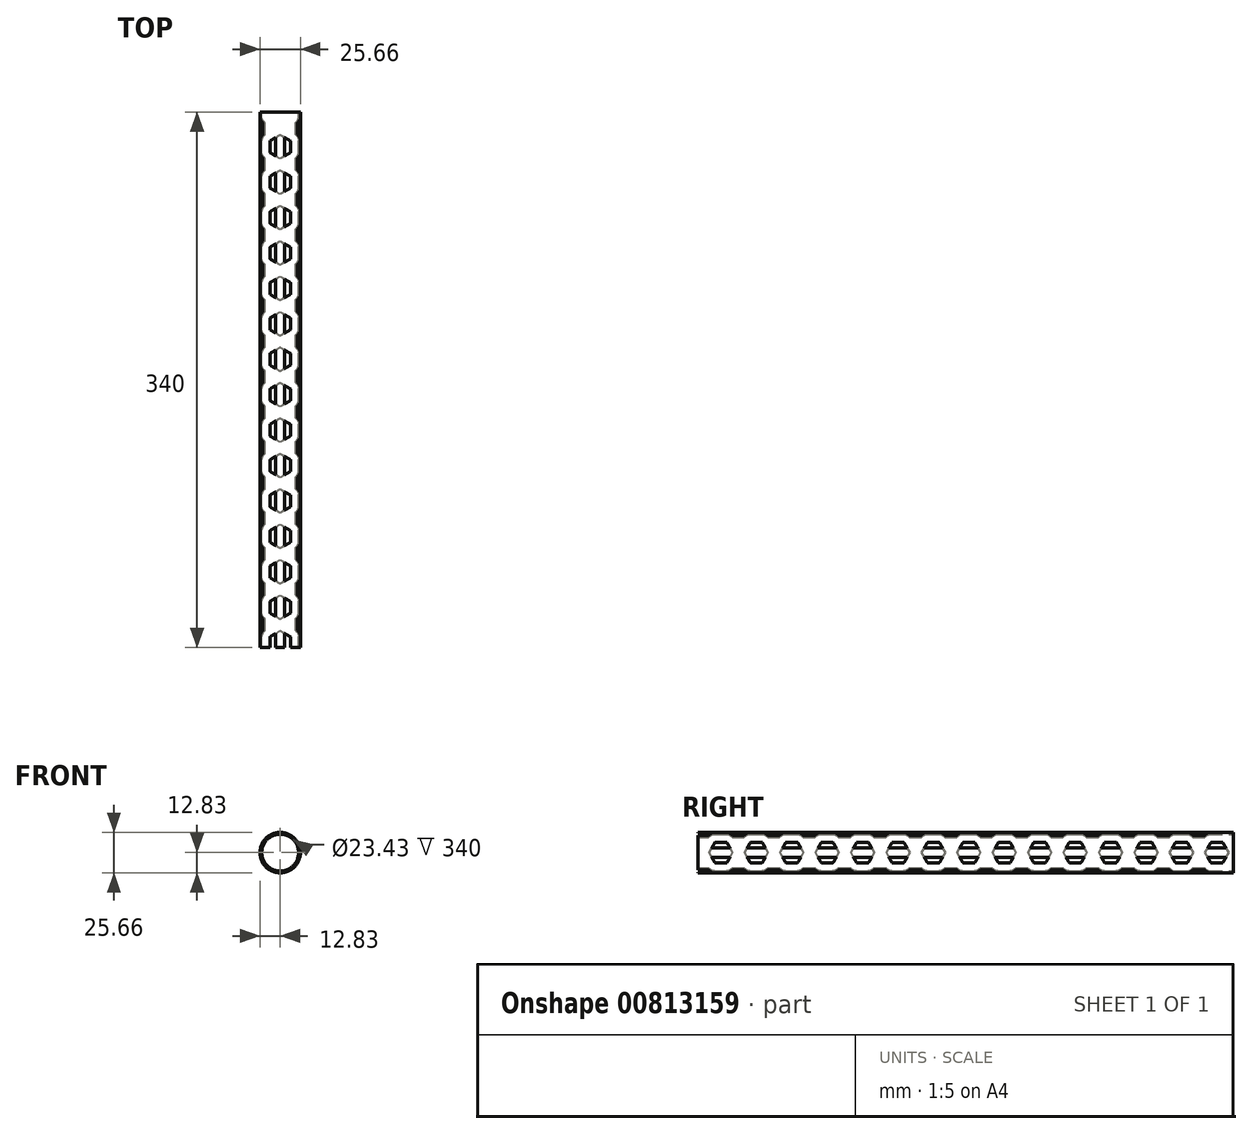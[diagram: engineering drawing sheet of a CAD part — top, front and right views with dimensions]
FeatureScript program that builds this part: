
annotation { "Feature Type Name" : "Feature", "Feature Type Description" : "" }
export const myFeature = defineFeature(function(context is Context, id is Id, definition is map)
    precondition{}
    {
        {
            var Q0;
            Q0=qCreatedBy(makeId("Front.planeOp"),FACE);
            var sketch = newSketch(context, id + "F0", { "sketchPlane" : qUnion([Q0])});
            skCircle(sketch, "E0", {"center": v(0, 0) * mm, "radius": 12.83 * mm});
            skCircle(sketch, "E1", {"center": v(0, 0) * mm, "radius": 11.72 * mm});
            skSolve(sketch);
        }
        {
            var Q0;
            Q0=makeQuery(id+"F0.imprint","IMPRINT",FACE,{"disambiguationData":[TD([[makeQuery(id+"F0.imprint","IMPRINT",EDGE,{"derivedFrom":sQuery(id+"F0.wireOp",EDGE,"E0")}),1.0]])]});
            var Q1;
            Q1=sQuery(id+"F0.wireOp",EDGE,"E1");
            var Q2;
            Q2=sQuery(id+"F0.wireOp",EDGE,"E0");
            extrude(context, id + "F1", {"entities" : qUnion([Q0]), "surfaceEntities" : qUnion([Q1, Q2]), "endBound" : BoundingType.SYMMETRIC, "depth" : 340 * mm, "offsetDistance" : 25 * mm});
        }
        {
            var Q0;
            Q0=qCreatedBy(makeId("Right.planeOp"),FACE);
            var sketch = newSketch(context, id + "F2", { "sketchPlane" : qUnion([Q0])});
            skCircle(sketch, "E2.cCircle", {"center": v(159.5, 0) * mm, "radius": 6.5 * mm, "construction": true});
            skLineSegment(sketch, "E2.0", {"start": v(155.75, 6.5) * mm, "end": v(163.25, 6.5) * mm});
            skLineSegment(sketch, "E2.1", {"start": v(163.25, 6.5) * mm, "end": v(167, 0) * mm});
            skLineSegment(sketch, "E2.2", {"start": v(167, 0) * mm, "end": v(163.25, -6.5) * mm});
            skLineSegment(sketch, "E2.3", {"start": v(163.25, -6.5) * mm, "end": v(155.75, -6.5) * mm});
            skLineSegment(sketch, "E2.4", {"start": v(155.75, -6.5) * mm, "end": v(152, 0) * mm});
            skLineSegment(sketch, "E2.5", {"start": v(152, 0) * mm, "end": v(155.75, 6.5) * mm});
            skPoint(sketch, "E2.0.midPoint", {"position": v(159.5, 6.5) * mm});
            skCircle(sketch, "E3.cCircle", {"center": v(137, 0) * mm, "radius": 6.5 * mm, "construction": true});
            skLineSegment(sketch, "E3.0", {"start": v(133.25, 6.5) * mm, "end": v(140.75, 6.5) * mm});
            skLineSegment(sketch, "E3.1", {"start": v(140.75, 6.5) * mm, "end": v(144.5, 0) * mm});
            skLineSegment(sketch, "E3.2", {"start": v(144.5, 0) * mm, "end": v(140.75, -6.5) * mm});
            skLineSegment(sketch, "E3.3", {"start": v(140.75, -6.5) * mm, "end": v(133.25, -6.5) * mm});
            skLineSegment(sketch, "E3.4", {"start": v(133.25, -6.5) * mm, "end": v(129.5, 0) * mm});
            skLineSegment(sketch, "E3.5", {"start": v(129.5, 0) * mm, "end": v(133.25, 6.5) * mm});
            skPoint(sketch, "E3.0.midPoint", {"position": v(137, 6.5) * mm});
            skCircle(sketch, "E4.cCircle", {"center": v(114.5, 0) * mm, "radius": 6.5 * mm, "construction": true});
            skLineSegment(sketch, "E4.0", {"start": v(110.75, 6.5) * mm, "end": v(118.25, 6.5) * mm});
            skLineSegment(sketch, "E4.1", {"start": v(118.25, 6.5) * mm, "end": v(122, 0) * mm});
            skLineSegment(sketch, "E4.2", {"start": v(122, 0) * mm, "end": v(118.25, -6.5) * mm});
            skLineSegment(sketch, "E4.3", {"start": v(118.25, -6.5) * mm, "end": v(110.75, -6.5) * mm});
            skLineSegment(sketch, "E4.4", {"start": v(110.75, -6.5) * mm, "end": v(107, 0) * mm});
            skLineSegment(sketch, "E4.5", {"start": v(107, 0) * mm, "end": v(110.75, 6.5) * mm});
            skPoint(sketch, "E4.0.midPoint", {"position": v(114.5, 6.5) * mm});
            skCircle(sketch, "E5.cCircle", {"center": v(92, 0) * mm, "radius": 6.5 * mm, "construction": true});
            skLineSegment(sketch, "E5.0", {"start": v(88.25, 6.5) * mm, "end": v(95.75, 6.5) * mm});
            skLineSegment(sketch, "E5.1", {"start": v(95.75, 6.5) * mm, "end": v(99.5, 0) * mm});
            skLineSegment(sketch, "E5.2", {"start": v(99.5, 0) * mm, "end": v(95.75, -6.5) * mm});
            skLineSegment(sketch, "E5.3", {"start": v(95.75, -6.5) * mm, "end": v(88.25, -6.5) * mm});
            skLineSegment(sketch, "E5.4", {"start": v(88.25, -6.5) * mm, "end": v(84.5, 0) * mm});
            skLineSegment(sketch, "E5.5", {"start": v(84.5, 0) * mm, "end": v(88.25, 6.5) * mm});
            skPoint(sketch, "E5.0.midPoint", {"position": v(92, 6.5) * mm});
            skCircle(sketch, "E6.cCircle", {"center": v(69.5, 0) * mm, "radius": 6.5 * mm, "construction": true});
            skLineSegment(sketch, "E6.0", {"start": v(65.75, 6.5) * mm, "end": v(73.25, 6.5) * mm});
            skLineSegment(sketch, "E6.1", {"start": v(73.25, 6.5) * mm, "end": v(77, 0) * mm});
            skLineSegment(sketch, "E6.2", {"start": v(77, 0) * mm, "end": v(73.25, -6.5) * mm});
            skLineSegment(sketch, "E6.3", {"start": v(73.25, -6.5) * mm, "end": v(65.75, -6.5) * mm});
            skLineSegment(sketch, "E6.4", {"start": v(65.75, -6.5) * mm, "end": v(62, 0) * mm});
            skLineSegment(sketch, "E6.5", {"start": v(62, 0) * mm, "end": v(65.75, 6.5) * mm});
            skPoint(sketch, "E6.0.midPoint", {"position": v(69.5, 6.5) * mm});
            skCircle(sketch, "E7.cCircle", {"center": v(47, 0) * mm, "radius": 6.5 * mm, "construction": true});
            skLineSegment(sketch, "E7.0", {"start": v(43.25, 6.5) * mm, "end": v(50.75, 6.5) * mm});
            skLineSegment(sketch, "E7.1", {"start": v(50.75, 6.5) * mm, "end": v(54.5, 0) * mm});
            skLineSegment(sketch, "E7.2", {"start": v(54.5, 0) * mm, "end": v(50.75, -6.5) * mm});
            skLineSegment(sketch, "E7.3", {"start": v(50.75, -6.5) * mm, "end": v(43.25, -6.5) * mm});
            skLineSegment(sketch, "E7.4", {"start": v(43.25, -6.5) * mm, "end": v(39.5, 0) * mm});
            skLineSegment(sketch, "E7.5", {"start": v(39.5, 0) * mm, "end": v(43.25, 6.5) * mm});
            skPoint(sketch, "E7.0.midPoint", {"position": v(47, 6.5) * mm});
            skCircle(sketch, "E8.cCircle", {"center": v(24.5, 0) * mm, "radius": 6.5 * mm, "construction": true});
            skLineSegment(sketch, "E8.0", {"start": v(20.75, 6.5) * mm, "end": v(28.25, 6.5) * mm});
            skLineSegment(sketch, "E8.1", {"start": v(28.25, 6.5) * mm, "end": v(32, 0) * mm});
            skLineSegment(sketch, "E8.2", {"start": v(32, 0) * mm, "end": v(28.25, -6.5) * mm});
            skLineSegment(sketch, "E8.3", {"start": v(28.25, -6.5) * mm, "end": v(20.75, -6.5) * mm});
            skLineSegment(sketch, "E8.4", {"start": v(20.75, -6.5) * mm, "end": v(17, 0) * mm});
            skLineSegment(sketch, "E8.5", {"start": v(17, 0) * mm, "end": v(20.75, 6.5) * mm});
            skPoint(sketch, "E8.0.midPoint", {"position": v(24.5, 6.5) * mm});
            skCircle(sketch, "E9.cCircle", {"center": v(2, 0) * mm, "radius": 6.5 * mm, "construction": true});
            skLineSegment(sketch, "E9.0", {"start": v(-1.75, 6.5) * mm, "end": v(5.75, 6.5) * mm});
            skLineSegment(sketch, "E9.1", {"start": v(5.75, 6.5) * mm, "end": v(9.5, 0) * mm});
            skLineSegment(sketch, "E9.2", {"start": v(9.5, 0) * mm, "end": v(5.75, -6.5) * mm});
            skLineSegment(sketch, "E9.3", {"start": v(5.75, -6.5) * mm, "end": v(-1.75, -6.5) * mm});
            skLineSegment(sketch, "E9.4", {"start": v(-1.75, -6.5) * mm, "end": v(-5.5, 0) * mm});
            skLineSegment(sketch, "E9.5", {"start": v(-5.5, 0) * mm, "end": v(-1.75, 6.5) * mm});
            skPoint(sketch, "E9.0.midPoint", {"position": v(2, 6.5) * mm});
            skCircle(sketch, "E10.cCircle", {"center": v(-20.5, 0) * mm, "radius": 6.5 * mm, "construction": true});
            skLineSegment(sketch, "E10.0", {"start": v(-24.25, 6.5) * mm, "end": v(-16.75, 6.5) * mm});
            skLineSegment(sketch, "E10.1", {"start": v(-16.75, 6.5) * mm, "end": v(-13, 0) * mm});
            skLineSegment(sketch, "E10.2", {"start": v(-13, 0) * mm, "end": v(-16.75, -6.5) * mm});
            skLineSegment(sketch, "E10.3", {"start": v(-16.75, -6.5) * mm, "end": v(-24.25, -6.5) * mm});
            skLineSegment(sketch, "E10.4", {"start": v(-24.25, -6.5) * mm, "end": v(-28, 0) * mm});
            skLineSegment(sketch, "E10.5", {"start": v(-28, 0) * mm, "end": v(-24.25, 6.5) * mm});
            skPoint(sketch, "E10.0.midPoint", {"position": v(-20.5, 6.5) * mm});
            skCircle(sketch, "E11.cCircle", {"center": v(-43, 0) * mm, "radius": 6.5 * mm, "construction": true});
            skLineSegment(sketch, "E11.0", {"start": v(-46.75, 6.5) * mm, "end": v(-39.25, 6.5) * mm});
            skLineSegment(sketch, "E11.1", {"start": v(-39.25, 6.5) * mm, "end": v(-35.5, 0) * mm});
            skLineSegment(sketch, "E11.2", {"start": v(-35.5, 0) * mm, "end": v(-39.25, -6.5) * mm});
            skLineSegment(sketch, "E11.3", {"start": v(-39.25, -6.5) * mm, "end": v(-46.75, -6.5) * mm});
            skLineSegment(sketch, "E11.4", {"start": v(-46.75, -6.5) * mm, "end": v(-50.5, 0) * mm});
            skLineSegment(sketch, "E11.5", {"start": v(-50.5, 0) * mm, "end": v(-46.75, 6.5) * mm});
            skPoint(sketch, "E11.0.midPoint", {"position": v(-43, 6.5) * mm});
            skCircle(sketch, "E12.cCircle", {"center": v(-65.5, 0) * mm, "radius": 6.5 * mm, "construction": true});
            skLineSegment(sketch, "E12.0", {"start": v(-69.25, 6.5) * mm, "end": v(-61.75, 6.5) * mm});
            skLineSegment(sketch, "E12.1", {"start": v(-61.75, 6.5) * mm, "end": v(-58, 0) * mm});
            skLineSegment(sketch, "E12.2", {"start": v(-58, 0) * mm, "end": v(-61.75, -6.5) * mm});
            skLineSegment(sketch, "E12.3", {"start": v(-61.75, -6.5) * mm, "end": v(-69.25, -6.5) * mm});
            skLineSegment(sketch, "E12.4", {"start": v(-69.25, -6.5) * mm, "end": v(-73, 0) * mm});
            skLineSegment(sketch, "E12.5", {"start": v(-73, 0) * mm, "end": v(-69.25, 6.5) * mm});
            skPoint(sketch, "E12.0.midPoint", {"position": v(-65.5, 6.5) * mm});
            skCircle(sketch, "E13.cCircle", {"center": v(-88, 0) * mm, "radius": 6.5 * mm, "construction": true});
            skLineSegment(sketch, "E13.0", {"start": v(-91.75, 6.5) * mm, "end": v(-84.25, 6.5) * mm});
            skLineSegment(sketch, "E13.1", {"start": v(-84.25, 6.5) * mm, "end": v(-80.5, 0) * mm});
            skLineSegment(sketch, "E13.2", {"start": v(-80.5, 0) * mm, "end": v(-84.25, -6.5) * mm});
            skLineSegment(sketch, "E13.3", {"start": v(-84.25, -6.5) * mm, "end": v(-91.75, -6.5) * mm});
            skLineSegment(sketch, "E13.4", {"start": v(-91.75, -6.5) * mm, "end": v(-95.5, 0) * mm});
            skLineSegment(sketch, "E13.5", {"start": v(-95.5, 0) * mm, "end": v(-91.75, 6.5) * mm});
            skPoint(sketch, "E13.0.midPoint", {"position": v(-88, 6.5) * mm});
            skCircle(sketch, "E14.cCircle", {"center": v(-110.5, 0) * mm, "radius": 6.5 * mm, "construction": true});
            skLineSegment(sketch, "E14.0", {"start": v(-114.25, 6.5) * mm, "end": v(-106.75, 6.5) * mm});
            skLineSegment(sketch, "E14.1", {"start": v(-106.75, 6.5) * mm, "end": v(-103, 0) * mm});
            skLineSegment(sketch, "E14.2", {"start": v(-103, 0) * mm, "end": v(-106.75, -6.5) * mm});
            skLineSegment(sketch, "E14.3", {"start": v(-106.75, -6.5) * mm, "end": v(-114.25, -6.5) * mm});
            skLineSegment(sketch, "E14.4", {"start": v(-114.25, -6.5) * mm, "end": v(-118, 0) * mm});
            skLineSegment(sketch, "E14.5", {"start": v(-118, 0) * mm, "end": v(-114.25, 6.5) * mm});
            skPoint(sketch, "E14.0.midPoint", {"position": v(-110.5, 6.5) * mm});
            skCircle(sketch, "E15.cCircle", {"center": v(-133, 0) * mm, "radius": 6.5 * mm, "construction": true});
            skLineSegment(sketch, "E15.0", {"start": v(-136.75, 6.5) * mm, "end": v(-129.25, 6.5) * mm});
            skLineSegment(sketch, "E15.1", {"start": v(-129.25, 6.5) * mm, "end": v(-125.5, 0) * mm});
            skLineSegment(sketch, "E15.2", {"start": v(-125.5, 0) * mm, "end": v(-129.25, -6.5) * mm});
            skLineSegment(sketch, "E15.3", {"start": v(-129.25, -6.5) * mm, "end": v(-136.75, -6.5) * mm});
            skLineSegment(sketch, "E15.4", {"start": v(-136.75, -6.5) * mm, "end": v(-140.5, 0) * mm});
            skLineSegment(sketch, "E15.5", {"start": v(-140.5, 0) * mm, "end": v(-136.75, 6.5) * mm});
            skPoint(sketch, "E15.0.midPoint", {"position": v(-133, 6.5) * mm});
            skCircle(sketch, "E16.cCircle", {"center": v(-155.5, 0) * mm, "radius": 6.5 * mm, "construction": true});
            skLineSegment(sketch, "E16.0", {"start": v(-159.25, 6.5) * mm, "end": v(-151.75, 6.5) * mm});
            skLineSegment(sketch, "E16.1", {"start": v(-151.75, 6.5) * mm, "end": v(-148, 0) * mm});
            skLineSegment(sketch, "E16.2", {"start": v(-148, 0) * mm, "end": v(-151.75, -6.5) * mm});
            skLineSegment(sketch, "E16.3", {"start": v(-151.75, -6.5) * mm, "end": v(-159.25, -6.5) * mm});
            skLineSegment(sketch, "E16.4", {"start": v(-159.25, -6.5) * mm, "end": v(-163, 0) * mm});
            skLineSegment(sketch, "E16.5", {"start": v(-163, 0) * mm, "end": v(-159.25, 6.5) * mm});
            skPoint(sketch, "E16.0.midPoint", {"position": v(-155.5, 6.5) * mm});
            skSolve(sketch);
        }
        {
            var Q0;
            Q0 = qSketchRegion(id + "F2", true);
            extrude(context, id + "F3", {"entities" : qUnion([Q0]), "operationType" : NewBodyOperationType.REMOVE, "endBound" : BoundingType.SYMMETRIC, "depth" : 25 * mm, "offsetDistance" : 25 * mm});
        }
        {
            var Q0;
            Q0=qCreatedBy(makeId("Top.planeOp"),FACE);
            var sketch = newSketch(context, id + "F4", { "sketchPlane" : qUnion([Q0])});
            skCircle(sketch, "E17.cCircle", {"center": v(0, -166.98) * mm, "radius": 6.5 * mm, "construction": true});
            skLineSegment(sketch, "E17.0", {"start": v(6.5, -163.23) * mm, "end": v(6.5, -170.73) * mm});
            skLineSegment(sketch, "E17.1", {"start": v(6.5, -170.73) * mm, "end": v(0, -174.48) * mm});
            skLineSegment(sketch, "E17.2", {"start": v(0, -174.48) * mm, "end": v(-6.5, -170.73) * mm});
            skLineSegment(sketch, "E17.3", {"start": v(-6.5, -170.73) * mm, "end": v(-6.5, -163.23) * mm});
            skLineSegment(sketch, "E17.4", {"start": v(-6.5, -163.23) * mm, "end": v(0, -159.48) * mm});
            skLineSegment(sketch, "E17.5", {"start": v(0, -159.48) * mm, "end": v(6.5, -163.23) * mm});
            skPoint(sketch, "E17.0.midPoint", {"position": v(6.5, -166.98) * mm});
            skCircle(sketch, "E18.cCircle", {"center": v(0, -144.48) * mm, "radius": 6.5 * mm, "construction": true});
            skLineSegment(sketch, "E18.0", {"start": v(6.5, -140.73) * mm, "end": v(6.5, -148.23) * mm});
            skLineSegment(sketch, "E18.1", {"start": v(6.5, -148.23) * mm, "end": v(0, -151.98) * mm});
            skLineSegment(sketch, "E18.2", {"start": v(0, -151.98) * mm, "end": v(-6.5, -148.23) * mm});
            skLineSegment(sketch, "E18.3", {"start": v(-6.5, -148.23) * mm, "end": v(-6.5, -140.73) * mm});
            skLineSegment(sketch, "E18.4", {"start": v(-6.5, -140.73) * mm, "end": v(0, -136.98) * mm});
            skLineSegment(sketch, "E18.5", {"start": v(0, -136.98) * mm, "end": v(6.5, -140.73) * mm});
            skPoint(sketch, "E18.0.midPoint", {"position": v(6.5, -144.48) * mm});
            skCircle(sketch, "E19.cCircle", {"center": v(0, -121.98) * mm, "radius": 6.5 * mm, "construction": true});
            skLineSegment(sketch, "E19.0", {"start": v(6.5, -118.23) * mm, "end": v(6.5, -125.73) * mm});
            skLineSegment(sketch, "E19.1", {"start": v(6.5, -125.73) * mm, "end": v(0, -129.48) * mm});
            skLineSegment(sketch, "E19.2", {"start": v(0, -129.48) * mm, "end": v(-6.5, -125.73) * mm});
            skLineSegment(sketch, "E19.3", {"start": v(-6.5, -125.73) * mm, "end": v(-6.5, -118.23) * mm});
            skLineSegment(sketch, "E19.4", {"start": v(-6.5, -118.23) * mm, "end": v(0, -114.48) * mm});
            skLineSegment(sketch, "E19.5", {"start": v(0, -114.48) * mm, "end": v(6.5, -118.23) * mm});
            skPoint(sketch, "E19.0.midPoint", {"position": v(6.5, -121.98) * mm});
            skCircle(sketch, "E20.cCircle", {"center": v(0, -99.48) * mm, "radius": 6.5 * mm, "construction": true});
            skLineSegment(sketch, "E20.0", {"start": v(6.5, -95.73) * mm, "end": v(6.5, -103.23) * mm});
            skLineSegment(sketch, "E20.1", {"start": v(6.5, -103.23) * mm, "end": v(0, -106.98) * mm});
            skLineSegment(sketch, "E20.2", {"start": v(0, -106.98) * mm, "end": v(-6.5, -103.23) * mm});
            skLineSegment(sketch, "E20.3", {"start": v(-6.5, -103.23) * mm, "end": v(-6.5, -95.73) * mm});
            skLineSegment(sketch, "E20.4", {"start": v(-6.5, -95.73) * mm, "end": v(0, -91.98) * mm});
            skLineSegment(sketch, "E20.5", {"start": v(0, -91.98) * mm, "end": v(6.5, -95.73) * mm});
            skPoint(sketch, "E20.0.midPoint", {"position": v(6.5, -99.48) * mm});
            skCircle(sketch, "E21.cCircle", {"center": v(0, -76.98) * mm, "radius": 6.5 * mm, "construction": true});
            skLineSegment(sketch, "E21.0", {"start": v(6.5, -73.23) * mm, "end": v(6.5, -80.73) * mm});
            skLineSegment(sketch, "E21.1", {"start": v(6.5, -80.73) * mm, "end": v(0, -84.48) * mm});
            skLineSegment(sketch, "E21.2", {"start": v(0, -84.48) * mm, "end": v(-6.5, -80.73) * mm});
            skLineSegment(sketch, "E21.3", {"start": v(-6.5, -80.73) * mm, "end": v(-6.5, -73.23) * mm});
            skLineSegment(sketch, "E21.4", {"start": v(-6.5, -73.23) * mm, "end": v(0, -69.48) * mm});
            skLineSegment(sketch, "E21.5", {"start": v(0, -69.48) * mm, "end": v(6.5, -73.23) * mm});
            skPoint(sketch, "E21.0.midPoint", {"position": v(6.5, -76.98) * mm});
            skCircle(sketch, "E22.cCircle", {"center": v(0, -54.48) * mm, "radius": 6.5 * mm, "construction": true});
            skLineSegment(sketch, "E22.0", {"start": v(6.5, -50.73) * mm, "end": v(6.5, -58.23) * mm});
            skLineSegment(sketch, "E22.1", {"start": v(6.5, -58.23) * mm, "end": v(0, -61.98) * mm});
            skLineSegment(sketch, "E22.2", {"start": v(0, -61.98) * mm, "end": v(-6.5, -58.23) * mm});
            skLineSegment(sketch, "E22.3", {"start": v(-6.5, -58.23) * mm, "end": v(-6.5, -50.73) * mm});
            skLineSegment(sketch, "E22.4", {"start": v(-6.5, -50.73) * mm, "end": v(0, -46.98) * mm});
            skLineSegment(sketch, "E22.5", {"start": v(0, -46.98) * mm, "end": v(6.5, -50.73) * mm});
            skPoint(sketch, "E22.0.midPoint", {"position": v(6.5, -54.48) * mm});
            skCircle(sketch, "E23.cCircle", {"center": v(0, -31.98) * mm, "radius": 6.5 * mm, "construction": true});
            skLineSegment(sketch, "E23.0", {"start": v(6.5, -28.23) * mm, "end": v(6.5, -35.73) * mm});
            skLineSegment(sketch, "E23.1", {"start": v(6.5, -35.73) * mm, "end": v(0, -39.48) * mm});
            skLineSegment(sketch, "E23.2", {"start": v(0, -39.48) * mm, "end": v(-6.5, -35.73) * mm});
            skLineSegment(sketch, "E23.3", {"start": v(-6.5, -35.73) * mm, "end": v(-6.5, -28.23) * mm});
            skLineSegment(sketch, "E23.4", {"start": v(-6.5, -28.23) * mm, "end": v(0, -24.48) * mm});
            skLineSegment(sketch, "E23.5", {"start": v(0, -24.48) * mm, "end": v(6.5, -28.23) * mm});
            skPoint(sketch, "E23.0.midPoint", {"position": v(6.5, -31.98) * mm});
            skCircle(sketch, "E24.cCircle", {"center": v(0, -9.48) * mm, "radius": 6.5 * mm, "construction": true});
            skLineSegment(sketch, "E24.0", {"start": v(6.5, -5.73) * mm, "end": v(6.5, -13.23) * mm});
            skLineSegment(sketch, "E24.1", {"start": v(6.5, -13.23) * mm, "end": v(0, -16.98) * mm});
            skLineSegment(sketch, "E24.2", {"start": v(0, -16.98) * mm, "end": v(-6.5, -13.23) * mm});
            skLineSegment(sketch, "E24.3", {"start": v(-6.5, -13.23) * mm, "end": v(-6.5, -5.73) * mm});
            skLineSegment(sketch, "E24.4", {"start": v(-6.5, -5.73) * mm, "end": v(0, -1.98) * mm});
            skLineSegment(sketch, "E24.5", {"start": v(0, -1.98) * mm, "end": v(6.5, -5.73) * mm});
            skPoint(sketch, "E24.0.midPoint", {"position": v(6.5, -9.48) * mm});
            skCircle(sketch, "E25.cCircle", {"center": v(0, 13.02) * mm, "radius": 6.5 * mm, "construction": true});
            skLineSegment(sketch, "E25.0", {"start": v(6.5, 16.77) * mm, "end": v(6.5, 9.27) * mm});
            skLineSegment(sketch, "E25.1", {"start": v(6.5, 9.27) * mm, "end": v(0, 5.52) * mm});
            skLineSegment(sketch, "E25.2", {"start": v(0, 5.52) * mm, "end": v(-6.5, 9.27) * mm});
            skLineSegment(sketch, "E25.3", {"start": v(-6.5, 9.27) * mm, "end": v(-6.5, 16.77) * mm});
            skLineSegment(sketch, "E25.4", {"start": v(-6.5, 16.77) * mm, "end": v(0, 20.52) * mm});
            skLineSegment(sketch, "E25.5", {"start": v(0, 20.52) * mm, "end": v(6.5, 16.77) * mm});
            skPoint(sketch, "E25.0.midPoint", {"position": v(6.5, 13.02) * mm});
            skCircle(sketch, "E26.cCircle", {"center": v(0, 35.52) * mm, "radius": 6.5 * mm, "construction": true});
            skLineSegment(sketch, "E26.0", {"start": v(6.5, 39.27) * mm, "end": v(6.5, 31.77) * mm});
            skLineSegment(sketch, "E26.1", {"start": v(6.5, 31.77) * mm, "end": v(0, 28.02) * mm});
            skLineSegment(sketch, "E26.2", {"start": v(0, 28.02) * mm, "end": v(-6.5, 31.77) * mm});
            skLineSegment(sketch, "E26.3", {"start": v(-6.5, 31.77) * mm, "end": v(-6.5, 39.27) * mm});
            skLineSegment(sketch, "E26.4", {"start": v(-6.5, 39.27) * mm, "end": v(0, 43.02) * mm});
            skLineSegment(sketch, "E26.5", {"start": v(0, 43.02) * mm, "end": v(6.5, 39.27) * mm});
            skPoint(sketch, "E26.0.midPoint", {"position": v(6.5, 35.52) * mm});
            skCircle(sketch, "E27.cCircle", {"center": v(0, 58.02) * mm, "radius": 6.5 * mm, "construction": true});
            skLineSegment(sketch, "E27.0", {"start": v(6.5, 61.77) * mm, "end": v(6.5, 54.27) * mm});
            skLineSegment(sketch, "E27.1", {"start": v(6.5, 54.27) * mm, "end": v(0, 50.52) * mm});
            skLineSegment(sketch, "E27.2", {"start": v(0, 50.52) * mm, "end": v(-6.5, 54.27) * mm});
            skLineSegment(sketch, "E27.3", {"start": v(-6.5, 54.27) * mm, "end": v(-6.5, 61.77) * mm});
            skLineSegment(sketch, "E27.4", {"start": v(-6.5, 61.77) * mm, "end": v(0, 65.52) * mm});
            skLineSegment(sketch, "E27.5", {"start": v(0, 65.52) * mm, "end": v(6.5, 61.77) * mm});
            skPoint(sketch, "E27.0.midPoint", {"position": v(6.5, 58.02) * mm});
            skCircle(sketch, "E28.cCircle", {"center": v(0, 80.52) * mm, "radius": 6.5 * mm, "construction": true});
            skLineSegment(sketch, "E28.0", {"start": v(6.5, 84.27) * mm, "end": v(6.5, 76.77) * mm});
            skLineSegment(sketch, "E28.1", {"start": v(6.5, 76.77) * mm, "end": v(0, 73.02) * mm});
            skLineSegment(sketch, "E28.2", {"start": v(0, 73.02) * mm, "end": v(-6.5, 76.77) * mm});
            skLineSegment(sketch, "E28.3", {"start": v(-6.5, 76.77) * mm, "end": v(-6.5, 84.27) * mm});
            skLineSegment(sketch, "E28.4", {"start": v(-6.5, 84.27) * mm, "end": v(0, 88.02) * mm});
            skLineSegment(sketch, "E28.5", {"start": v(0, 88.02) * mm, "end": v(6.5, 84.27) * mm});
            skPoint(sketch, "E28.0.midPoint", {"position": v(6.5, 80.52) * mm});
            skCircle(sketch, "E29.cCircle", {"center": v(0, 103.02) * mm, "radius": 6.5 * mm, "construction": true});
            skLineSegment(sketch, "E29.0", {"start": v(6.5, 106.77) * mm, "end": v(6.5, 99.27) * mm});
            skLineSegment(sketch, "E29.1", {"start": v(6.5, 99.27) * mm, "end": v(0, 95.52) * mm});
            skLineSegment(sketch, "E29.2", {"start": v(0, 95.52) * mm, "end": v(-6.5, 99.27) * mm});
            skLineSegment(sketch, "E29.3", {"start": v(-6.5, 99.27) * mm, "end": v(-6.5, 106.77) * mm});
            skLineSegment(sketch, "E29.4", {"start": v(-6.5, 106.77) * mm, "end": v(0, 110.52) * mm});
            skLineSegment(sketch, "E29.5", {"start": v(0, 110.52) * mm, "end": v(6.5, 106.77) * mm});
            skPoint(sketch, "E29.0.midPoint", {"position": v(6.5, 103.02) * mm});
            skCircle(sketch, "E30.cCircle", {"center": v(0, 125.52) * mm, "radius": 6.5 * mm, "construction": true});
            skLineSegment(sketch, "E30.0", {"start": v(6.5, 129.27) * mm, "end": v(6.5, 121.77) * mm});
            skLineSegment(sketch, "E30.1", {"start": v(6.5, 121.77) * mm, "end": v(0, 118.02) * mm});
            skLineSegment(sketch, "E30.2", {"start": v(0, 118.02) * mm, "end": v(-6.5, 121.77) * mm});
            skLineSegment(sketch, "E30.3", {"start": v(-6.5, 121.77) * mm, "end": v(-6.5, 129.27) * mm});
            skLineSegment(sketch, "E30.4", {"start": v(-6.5, 129.27) * mm, "end": v(0, 133.02) * mm});
            skLineSegment(sketch, "E30.5", {"start": v(0, 133.02) * mm, "end": v(6.5, 129.27) * mm});
            skPoint(sketch, "E30.0.midPoint", {"position": v(6.5, 125.52) * mm});
            skCircle(sketch, "E31.cCircle", {"center": v(0, 148.02) * mm, "radius": 6.5 * mm, "construction": true});
            skLineSegment(sketch, "E31.0", {"start": v(6.5, 151.77) * mm, "end": v(6.5, 144.27) * mm});
            skLineSegment(sketch, "E31.1", {"start": v(6.5, 144.27) * mm, "end": v(0, 140.52) * mm});
            skLineSegment(sketch, "E31.2", {"start": v(0, 140.52) * mm, "end": v(-6.5, 144.27) * mm});
            skLineSegment(sketch, "E31.3", {"start": v(-6.5, 144.27) * mm, "end": v(-6.5, 151.77) * mm});
            skLineSegment(sketch, "E31.4", {"start": v(-6.5, 151.77) * mm, "end": v(0, 155.52) * mm});
            skLineSegment(sketch, "E31.5", {"start": v(0, 155.52) * mm, "end": v(6.5, 151.77) * mm});
            skPoint(sketch, "E31.0.midPoint", {"position": v(6.5, 148.02) * mm});
            skSolve(sketch);
        }
        {
            var Q0;
            Q0 = qSketchRegion(id + "F4", true);
            extrude(context, id + "F5", {"entities" : qUnion([Q0]), "operationType" : NewBodyOperationType.REMOVE, "endBound" : BoundingType.SYMMETRIC, "oppositeDirection" : true, "depth" : 25 * mm, "offsetDistance" : 25 * mm});
        }
    });
